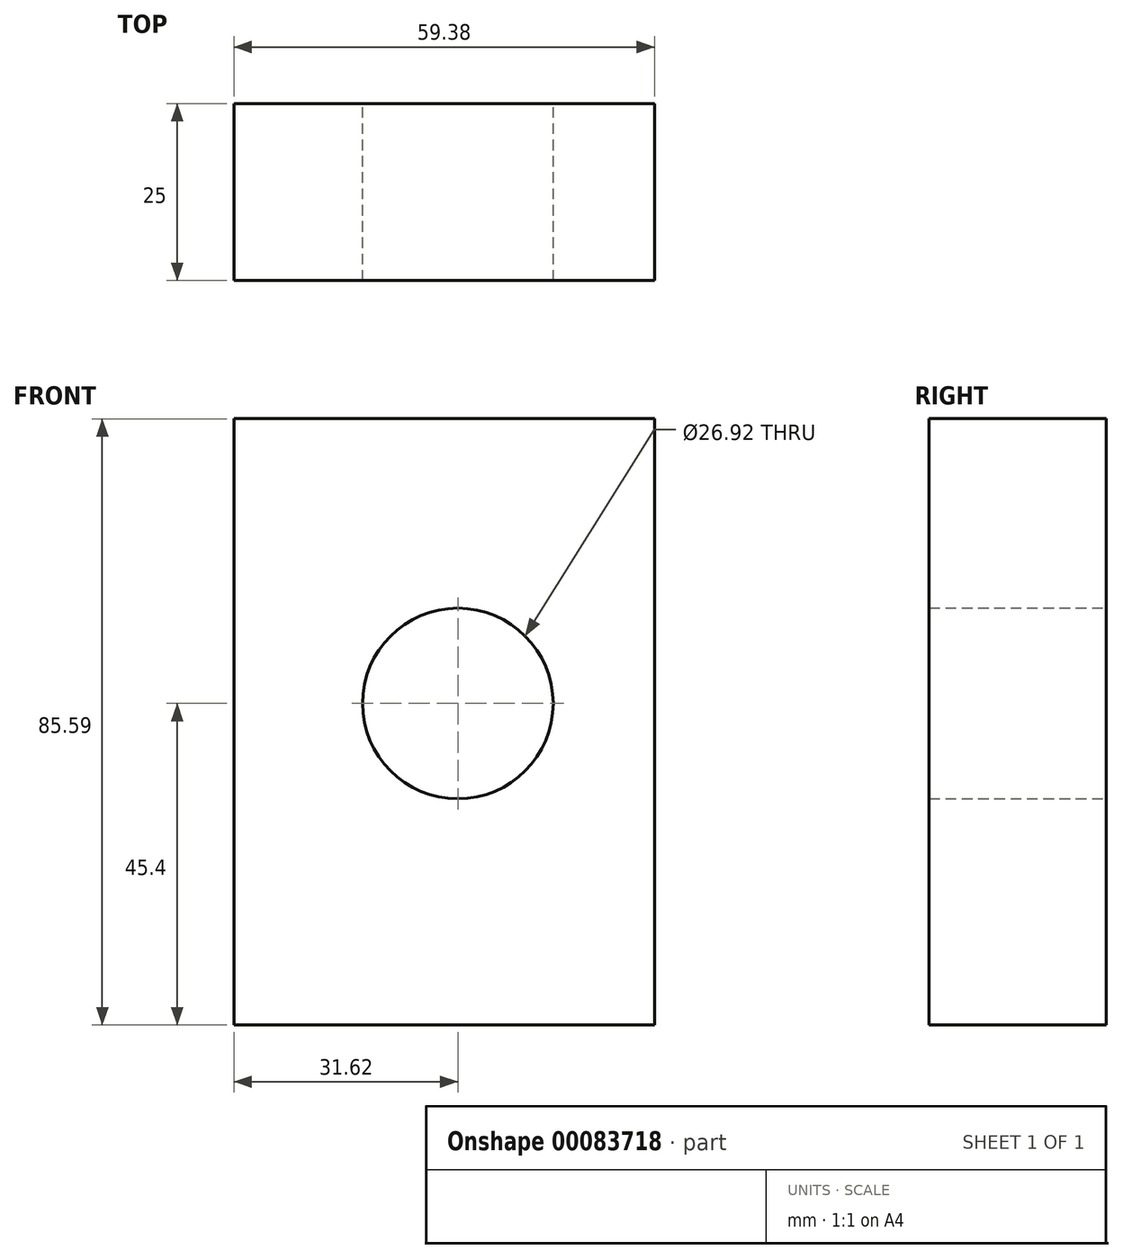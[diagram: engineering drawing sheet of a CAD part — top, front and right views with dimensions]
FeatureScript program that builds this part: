
annotation { "Feature Type Name" : "Feature", "Feature Type Description" : "" }
export const myFeature = defineFeature(function(context is Context, id is Id, definition is map)
    precondition{}
    {
        {
            var Q0;
            Q0=qCreatedBy(makeId("Front.planeOp"),FACE);
            var sketch = newSketch(context, id + "F0", { "sketchPlane" : qUnion([Q0])});
            skCircle(sketch, "E0", {"center": v(0, 0) * mm, "radius": 13.46 * mm});
            skLineSegment(sketch, "E1.bottom", {"start": v(-31.62, 40.2) * mm, "end": v(27.76, 40.2) * mm});
            skLineSegment(sketch, "E1.top", {"start": v(-31.62, -45.4) * mm, "end": v(27.76, -45.4) * mm});
            skLineSegment(sketch, "E1.left", {"start": v(-31.62, 40.2) * mm, "end": v(-31.62, -45.4) * mm});
            skLineSegment(sketch, "E1.right", {"start": v(27.76, 40.2) * mm, "end": v(27.76, -45.4) * mm});
            skSolve(sketch);
        }
        {
            var Q0;
            Q0 = qSketchRegion(id + "F0", true);
            extrude(context, id + "F1", {"entities" : qUnion([Q0]), "depth" : 25 * mm});
        }
    });
